# Revit family: Heat_Pump-Water_to_Water-Rheem--
name_source: partatom
category: Mechanical Equipment
units: mm (PartAtom-declared; Revit-internal decimal feet)

## family parameters
Always vertical = Yes
Cut with Voids When Loaded = No
OmniClass Number = 23.75.10.21.17
OmniClass Title = Water-Source Heat Pumps
Part Type = Normal
Room Calculation Point = No
Round Connector Dimension = Use Radius
Shared = No
Work Plane-Based = No

## types (1)
- ERROR_LOAD TYPE CATALOG
    Apparent Power = 24000 VA
    Assembly Code = D3040600
    Base Height = 100 mm  [stored 0.328084 ft]
    Chilled Water Pipe Horizontal Offset = 180 mm  [stored 0.590551 ft]
    Chilled Water Pipe Return Vertical Offset = 620 mm  [stored 2.03412 ft]
    Chilled Water Pipe Supply Vertical Offset = 900 mm  [stored 2.95276 ft]
    Cold Water Flow = 3.4 L/s
    Connection Size = 65 mm
    Cooling COP at 20C = 4.02
    Cooling Water Pressure Drop = 50.0 kPa
    DHW Pipe Horizontal Offset = 180 mm  [stored 0.590551 ft]
    DHW Retiurn Pipe Vertical Offset = 240 mm  [stored 0.787402 ft]
    DHW Supply Pipe Vertical Offset = 960 mm  [stored 3.14961 ft]
    Default Elevation = 0 mm  [stored 0 ft]
    Description = Water to Water Heat Pump
    ENGworks Global = www.ENGWorksGlobal.com
    Enclosure Height = 1100 mm
    Enclosure Length = 2120 mm  [stored 6.95538 ft]
    Enclosure Material = Metal - Rheem - Gray
    Enclosure Width = 805 mm  [stored 2.64108 ft]
    Flange Diameter = 185 mm  [stored 0.606955 ft]
    Flange Radius = 93 mm
    Flange Thickness = 18 mm  [stored 0.0590551 ft]
    Frequency = 50 Hz
    Front Clearance = 850 mm  [stored 2.78871 ft]
    Heat Exchanger Type = Shell in Tube
    Heating COP at 20C = 5.02
    Heating COP at 35C = 7.01
    Hot Water Flow = 4.4 L/s
    Left Clearance = 200 mm  [stored 0.656168 ft]
    Load Classification = HVAC
    Load Sub-Classification Motor = Yes
    Manufacturer = Rheem
    Maximum Cooling Water Pressure = 660.0 kPa
    Maximum DHW Temperature = 65 °C
    Maximum Overcurrent Protection = 40 A
    Minimum Circuit Amps = 50 A
    Model = 955071SDP
    Nominal Cooling Capacity at 20C = 4020 W
    Nominal Heating Capacity at 20C = 5020 W
    Nominal Heating Capacity at 35C = 7010 W
    Number of Poles = 1
    Phase = 1
    Pipe Diameter = 122 mm  [stored 0.400262 ft]
    Pipe Length = 140 mm
    Power Consumption = 14 kW
    Product Page URL = https://www.rheem.com.au
    Refrigerant Used = R134a
    Right Clearance = 200 mm  [stored 0.656168 ft]
    Top Clearance = 500 mm  [stored 1.64042 ft]
    URL = https://www.rheem.com.au
    Unit Weight = 0.00 kgf
    Unit Weight Value = 0
    Version = 1
    Voltage = 480 V
    Voltage Comments = 380 VAC - 415 VAC

note: [stored X ft] marks values corroborated as IEEE doubles in the binary element streams (Revit-internal decimal feet)

## geometry (parser evidence)
native form markers: Sweep x5
no freeform markers — native parametric forms only
